# Revit family: Gira_283203
name_source: partatom
category: Electrical Fixtures
revit_build: Autodesk Revit 2017 (Build: 20160225_1515(x64)
units: mm (PartAtom-declared; Revit-internal decimal feet)

## family parameters
Cut with Voids When Loaded = No
Host = Face
Maintain Annotation Orientation = Yes
Part Type = Normal
Room Calculation Point = No
Round Connector Dimension = Use Diameter
Shared = No

## types (1)
- Wippschalter 3f Wechselsch. System 55 Reinweiß
    Anschlussart = Schraubklemme
    Anzahl der Betätigungswippen = 3
    Anzahl der Module (bei Modulbauweise) = 1
    Available = Yes
    Bedienungsart = Wippe/Taste
    Befestigungsart = Schraubbefestigung
    Beleuchtung = nein
    Bemessungsstrom = 10 Ampere
    Category = Installationsschalter
    Data sheet (1) = https://katalog.gira.de
    Default Elevation = 1219 mm
    Farbe = weiß
    GTIN = 4010337832034
    Geeignet für Schutzart (IP) = IP20
    HAN = 283203
    Halogenfrei = Yes
    HeinzeBIM = https://bimportal.heinze.de
    Manufacturer URL = https://www.gira.de
    Mit Montageplatte = No
    Model = Sys55_Komplettgerät_Schalten und Tasten
    Montageart = unter Putz
    Name = Wippschalter 3f Wechselsch. System 55 Reinweiß
    Nennspannung = 250 Volt
    Oberfläche = sonstige
    RAL-Nummer (ähnlich) = 9010
    Region = DE
    Rückmeldekontakt = No
    Schaltungsart = Wechselschalter
    Tastschalter = No
    Textfeld/Beschriftungsfläche = nein
    URL = http://katalog.gira.de
    Waschmaschinenschalter = No
    Werkstoff = sonstige
    Werkstoffgüte = sonstige
    Zusammenstellung = Basiselement mit Adapterplatte

## geometry (parser evidence)
native form markers: Blend x2, Sweep x8
no freeform markers — native parametric forms only
